# Revit family: single booth
name_source: partatom
category: Furniture
revit_build: Autodesk Revit 2016 (Build: 20151209_0715(x64)
units: mm (PartAtom-declared; Revit-internal decimal feet)

## family parameters
Always vertical = Yes
Cut with Voids When Loaded = No
OmniClass Number = 23.40.20.00
OmniClass Title = General Furniture and Specialties
Room Calculation Point = No
Shared = No
Work Plane-Based = No

## types (15) — shared parameters
Width = 2' - 1"

## per-type parameters (varying)
| type | Description | Fabric | Frame | Height | Length | Seat Fabric | Type Comments |
| 48" x 36"H | Double Booth 48" Deep x 25" Wide x 42" Overall Height | <By Category> | <By Category> | 3' - 0" | 4' - 0" | <By Category> | Outside finished end on front right side only. Backs upholstered with 5 rows of buttons sewn in deep diamond tufts; upholstery to be chocolate colored vinyl |
| 60" x 42"H |  | <By Category> | <By Category> | 3' - 6" | 5' - 0" | <By Category> |  |
| 24" x 42"H |  | <By Category> | <By Category> | 3' - 6" | 2' - 0" | <By Category> |  |
| 30" x 42"H | Double Booth 48" Deep x 25" Wide x 42" Overall Height | <By Category> | <By Category> | 3' - 0" | 2' - 6" | <By Category> | Outside finished end on front right side only. Backs upholstered with 5 rows of buttons sewn in deep diamond tufts; upholstery to be chocolate colored vinyl |
| 42" x 42"H | Double Booth 48" Deep x 25" Wide x 42" Overall Height | <By Category> | <By Category> | 3' - 6" | 3' - 6" | <By Category> | Outside finished end on front right side only. Backs upholstered with 5 rows of buttons sewn in deep diamond tufts; upholstery to be chocolate colored vinyl |
| 24" x 36"H |  | <By Category> | <By Category> | 3' - 0" | 2' - 0" | <By Category> |  |
| 48" x 42"H | Double Booth 48" Deep x 25" Wide x 42" Overall Height | WYO_F-2_Booth Back | Fabric- Bernhardt Design - Leather - Black | 3' - 6" | 4' - 0" | WYO_F-1_Fabric | Outside finished end on front right side only. Backs upholstered with 5 rows of buttons sewn in deep diamond tufts; upholstery to be chocolate colored vinyl |
| 60" x 36"H |  | <By Category> | <By Category> | 3' - 0" | 5' - 0" | <By Category> |  |
| 30" x 36"H | Double Booth 48" Deep x 25" Wide x 42" Overall Height | <By Category> | <By Category> | 3' - 0" | 2' - 6" | <By Category> | Outside finished end on front right side only. Backs upholstered with 5 rows of buttons sewn in deep diamond tufts; upholstery to be chocolate colored vinyl |
| 42" x 36"H | Double Booth 48" Deep x 25" Wide x 42" Overall Height | <By Category> | <By Category> | 3' - 0" | 3' - 6" | <By Category> | Outside finished end on front right side only. Backs upholstered with 5 rows of buttons sewn in deep diamond tufts; upholstery to be chocolate colored vinyl |
| 54" x 36"H | Double Booth 48" Deep x 25" Wide x 42" Overall Height | <By Category> | <By Category> | 3' - 0" | 4' - 6" | <By Category> | Outside finished end on front right side only. Backs upholstered with 5 rows of buttons sewn in deep diamond tufts; upholstery to be chocolate colored vinyl |
| 54" x 42"H | Double Booth 48" Deep x 25" Wide x 42" Overall Height | WYO_F-3_Booth Back | WYO_PL-1_FRP | 3' - 6" | 4' - 6" | <By Category> | Outside finished end on front right side only. Backs upholstered with 5 rows of buttons sewn in deep diamond tufts; upholstery to be chocolate colored vinyl |
| 36" x 42"H | Double Booth 48" Deep x 25" Wide x 42" Overall Height | WYO_F-2_Booth Back | WYO_PL-1_FRP | 3' - 6" | 3' - 0" | WYO_F-1_Fabric | Outside finished end on front right side only. Backs upholstered with 5 rows of buttons sewn in deep diamond tufts; upholstery to be chocolate colored vinyl |
| 36" x 36"H | Double Booth 48" Deep x 25" Wide x 42" Overall Height | <By Category> | <By Category> | 3' - 0" | 3' - 0" | <By Category> | Outside finished end on front right side only. Backs upholstered with 5 rows of buttons sewn in deep diamond tufts; upholstery to be chocolate colored vinyl |
| 72" x 42"H | Double Booth 48" Deep x 25" Wide x 42" Overall Height | WYO_F-3_Booth Back | WYO_PL-1_FRP | 3' - 6" | 6' - 0" | WYO_F-1_Fabric | Outside finished end on front right side only. Backs upholstered with 5 rows of buttons sewn in deep diamond tufts; upholstery to be chocolate colored vinyl |

## geometry (parser evidence)
native form markers: Blend x2, Sweep x2
no freeform markers — native parametric forms only
